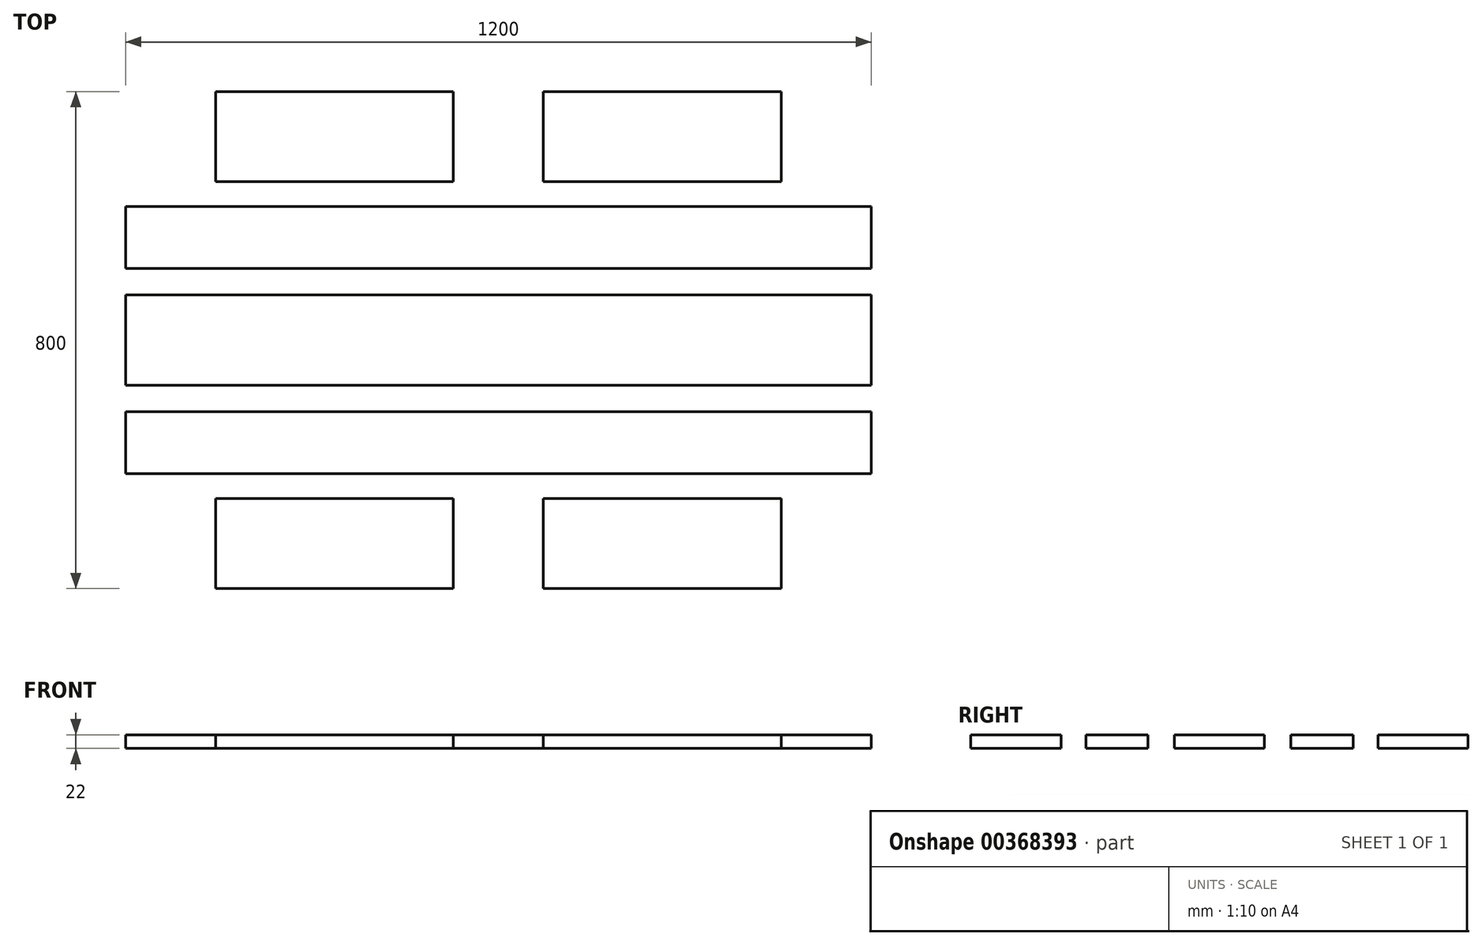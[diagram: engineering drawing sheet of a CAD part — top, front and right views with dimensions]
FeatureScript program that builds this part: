
annotation { "Feature Type Name" : "Feature", "Feature Type Description" : "" }
export const myFeature = defineFeature(function(context is Context, id is Id, definition is map)
    precondition{}
    {
        {
            var Q0;
            Q0=qCreatedBy(makeId("Top.planeOp"),FACE);
            var sketch = newSketch(context, id + "F0", { "sketchPlane" : qUnion([Q0])});
            skLineSegment(sketch, "E0.bottom", {"start": v(600, 400) * mm, "end": v(-600, 400) * mm, "construction": true});
            skLineSegment(sketch, "E0.top", {"start": v(600, -400) * mm, "end": v(-600, -400) * mm, "construction": true});
            skLineSegment(sketch, "E0.left", {"start": v(600, 400) * mm, "end": v(600, -400) * mm, "construction": true});
            skLineSegment(sketch, "E0.right", {"start": v(-600, 400) * mm, "end": v(-600, -400) * mm, "construction": true});
            skPoint(sketch, "E0.middle", {"position": v(0, 0) * mm});
            skLineSegment(sketch, "E1.left", {"start": v(-600, -400) * mm, "end": v(-600, -400) * mm});
            skLineSegment(sketch, "E1.right", {"start": v(600, -400) * mm, "end": v(600, -400) * mm});
            skLineSegment(sketch, "E2.bottom", {"start": v(-600, -400) * mm, "end": v(600, -400) * mm});
            skLineSegment(sketch, "E2.top", {"start": v(-600, -255) * mm, "end": v(600, -255) * mm});
            skLineSegment(sketch, "E2.left", {"start": v(-600, -400) * mm, "end": v(-600, -255) * mm});
            skLineSegment(sketch, "E2.right", {"start": v(600, -400) * mm, "end": v(600, -255) * mm});
            skLineSegment(sketch, "E3.bottom", {"start": v(-600, 400) * mm, "end": v(600, 400) * mm});
            skLineSegment(sketch, "E3.top", {"start": v(-600, 255) * mm, "end": v(600, 255) * mm});
            skLineSegment(sketch, "E3.left", {"start": v(-600, 400) * mm, "end": v(-600, 255) * mm});
            skLineSegment(sketch, "E3.right", {"start": v(600, 400) * mm, "end": v(600, 255) * mm});
            skLineSegment(sketch, "E4.bottom", {"start": v(-600, 72.5) * mm, "end": v(600, 72.5) * mm});
            skLineSegment(sketch, "E4.top", {"start": v(-600, -72.5) * mm, "end": v(600, -72.5) * mm});
            skLineSegment(sketch, "E4.left", {"start": v(-600, 72.5) * mm, "end": v(-600, -72.5) * mm});
            skLineSegment(sketch, "E4.right", {"start": v(600, 72.5) * mm, "end": v(600, -72.5) * mm});
            skLineSegment(sketch, "E5.bottom", {"start": v(-600, 215) * mm, "end": v(600, 215) * mm});
            skLineSegment(sketch, "E5.top", {"start": v(-600, 115) * mm, "end": v(600, 115) * mm});
            skLineSegment(sketch, "E5.left", {"start": v(-600, 215) * mm, "end": v(-600, 115) * mm});
            skLineSegment(sketch, "E5.right", {"start": v(600, 215) * mm, "end": v(600, 115) * mm});
            skLineSegment(sketch, "E6.bottom", {"start": v(-600, -115) * mm, "end": v(600, -115) * mm});
            skLineSegment(sketch, "E6.top", {"start": v(-600, -215) * mm, "end": v(600, -215) * mm});
            skLineSegment(sketch, "E6.left", {"start": v(-600, -115) * mm, "end": v(-600, -215) * mm});
            skLineSegment(sketch, "E6.right", {"start": v(600, -115) * mm, "end": v(600, -215) * mm});
            skLineSegment(sketch, "E7.bottom", {"start": v(-600, 400) * mm, "end": v(-455, 400) * mm});
            skLineSegment(sketch, "E7.top", {"start": v(-600, -400) * mm, "end": v(-455, -400) * mm});
            skLineSegment(sketch, "E7.left", {"start": v(-600, 400) * mm, "end": v(-600, -400) * mm});
            skLineSegment(sketch, "E7.right", {"start": v(-455, 400) * mm, "end": v(-455, -400) * mm});
            skLineSegment(sketch, "E8.bottom", {"start": v(600, 400) * mm, "end": v(455, 400) * mm});
            skLineSegment(sketch, "E8.top", {"start": v(600, -400) * mm, "end": v(455, -400) * mm});
            skLineSegment(sketch, "E8.left", {"start": v(600, 400) * mm, "end": v(600, -400) * mm});
            skLineSegment(sketch, "E8.right", {"start": v(455, 400) * mm, "end": v(455, -400) * mm});
            skLineSegment(sketch, "E9.bottom", {"start": v(72, -400) * mm, "end": v(-73, -400) * mm});
            skLineSegment(sketch, "E9.top", {"start": v(72, 400) * mm, "end": v(-73, 400) * mm});
            skLineSegment(sketch, "E9.left", {"start": v(72, -400) * mm, "end": v(72, 400) * mm});
            skLineSegment(sketch, "E9.right", {"start": v(-73, -400) * mm, "end": v(-73, 400) * mm});
            skPoint(sketch, "E9.middle", {"position": v(-0.5, 0) * mm});
            skSolve(sketch);
        }
        {
            var Q0;
            {var subQ5=sQuery(id+"F0.wireOp",EDGE,"E8.bottom");Q0=makeQuery(id+"F0.imprint","IMPRINT",FACE,{"disambiguationData":[TD([[makeQuery(id+"F0.imprint","IMPRINT",EDGE,{"derivedFrom":subQ5}),1.0]])]});}
            var Q1;
            {var subQ3=sQuery(id+"F0.wireOp",EDGE,"E9.left");var subQ5=sQuery(id+"F0.wireOp",EDGE,"E3.top");var subQ6=makeQuery(id+"F0.imprint","INTERSECT",VERTEX,{"derivedFrom":[subQ5,subQ3]});Q1=makeQuery(id+"F0.imprint","IMPRINT",FACE,{"disambiguationData":[TD([[makeQuery(id+"F0.imprint","IMPRINT",EDGE,{"disambiguationData":[TD([[subQ6,-1.0]])],"derivedFrom":subQ5}),1.0]])]});}
            var Q2;
            {var subQ5=sQuery(id+"F0.wireOp",EDGE,"E9.top");Q2=makeQuery(id+"F0.imprint","IMPRINT",FACE,{"disambiguationData":[TD([[makeQuery(id+"F0.imprint","IMPRINT",EDGE,{"derivedFrom":subQ5}),1.0]])]});}
            var Q3;
            {var subQ0=sQuery(id+"F0.wireOp",EDGE,"E7.right");var subQ5=sQuery(id+"F0.wireOp",EDGE,"E3.top");var subQ6=makeQuery(id+"F0.imprint","INTERSECT",VERTEX,{"derivedFrom":[subQ5,subQ0]});Q3=makeQuery(id+"F0.imprint","IMPRINT",FACE,{"disambiguationData":[TD([[makeQuery(id+"F0.imprint","IMPRINT",EDGE,{"disambiguationData":[TD([[subQ6,-1.0]])],"derivedFrom":subQ5}),1.0]])]});}
            var Q4;
            {var subQ5=sQuery(id+"F0.wireOp",EDGE,"E7.bottom");Q4=makeQuery(id+"F0.imprint","IMPRINT",FACE,{"disambiguationData":[TD([[makeQuery(id+"F0.imprint","IMPRINT",EDGE,{"derivedFrom":subQ5}),-1.0]])]});}
            var Q5;
            {var subQ0=sQuery(id+"F0.wireOp",EDGE,"E7.left");var subQ1=sQuery(id+"F0.wireOp",EDGE,"E5.bottom");var subQ2=makeQuery(id+"F0.imprint","INTERSECT",VERTEX,{"derivedFrom":[subQ1,subQ0]});Q5=makeQuery(id+"F0.imprint","IMPRINT",FACE,{"disambiguationData":[TD([[makeQuery(id+"F0.imprint","IMPRINT",EDGE,{"disambiguationData":[TD([[subQ2,-1.0]])],"derivedFrom":subQ1}),-1.0]])]});}
            var Q6;
            {var subQ0=sQuery(id+"F0.wireOp",EDGE,"E7.right");var subQ1=sQuery(id+"F0.wireOp",EDGE,"E5.bottom");var subQ2=makeQuery(id+"F0.imprint","INTERSECT",VERTEX,{"derivedFrom":[subQ1,subQ0]});Q6=makeQuery(id+"F0.imprint","IMPRINT",FACE,{"disambiguationData":[TD([[makeQuery(id+"F0.imprint","IMPRINT",EDGE,{"disambiguationData":[TD([[subQ2,-1.0]])],"derivedFrom":subQ1}),-1.0]])]});}
            var Q7;
            {var subQ0=sQuery(id+"F0.wireOp",EDGE,"E9.right");var subQ1=sQuery(id+"F0.wireOp",EDGE,"E5.bottom");var subQ2=makeQuery(id+"F0.imprint","INTERSECT",VERTEX,{"derivedFrom":[subQ1,subQ0]});Q7=makeQuery(id+"F0.imprint","IMPRINT",FACE,{"disambiguationData":[TD([[makeQuery(id+"F0.imprint","IMPRINT",EDGE,{"disambiguationData":[TD([[subQ2,-1.0]])],"derivedFrom":subQ1}),-1.0]])]});}
            var Q8;
            {var subQ0=sQuery(id+"F0.wireOp",EDGE,"E9.left");var subQ1=sQuery(id+"F0.wireOp",EDGE,"E5.bottom");var subQ2=makeQuery(id+"F0.imprint","INTERSECT",VERTEX,{"derivedFrom":[subQ1,subQ0]});Q8=makeQuery(id+"F0.imprint","IMPRINT",FACE,{"disambiguationData":[TD([[makeQuery(id+"F0.imprint","IMPRINT",EDGE,{"disambiguationData":[TD([[subQ2,-1.0]])],"derivedFrom":subQ1}),-1.0]])]});}
            var Q9;
            {var subQ0=sQuery(id+"F0.wireOp",EDGE,"E8.left");var subQ1=sQuery(id+"F0.wireOp",EDGE,"E5.bottom");var subQ2=makeQuery(id+"F0.imprint","INTERSECT",VERTEX,{"derivedFrom":[subQ1,subQ0]});Q9=makeQuery(id+"F0.imprint","IMPRINT",FACE,{"disambiguationData":[TD([[makeQuery(id+"F0.imprint","IMPRINT",EDGE,{"disambiguationData":[TD([[subQ2,1.0]])],"derivedFrom":subQ1}),-1.0]])]});}
            var Q10;
            {var subQ0=sQuery(id+"F0.wireOp",EDGE,"E8.left");var subQ1=sQuery(id+"F0.wireOp",EDGE,"E4.bottom");var subQ2=makeQuery(id+"F0.imprint","INTERSECT",VERTEX,{"derivedFrom":[subQ1,subQ0]});Q10=makeQuery(id+"F0.imprint","IMPRINT",FACE,{"disambiguationData":[TD([[makeQuery(id+"F0.imprint","IMPRINT",EDGE,{"disambiguationData":[TD([[subQ2,1.0]])],"derivedFrom":subQ1}),-1.0]])]});}
            var Q11;
            {var subQ0=sQuery(id+"F0.wireOp",EDGE,"E9.left");var subQ1=sQuery(id+"F0.wireOp",EDGE,"E4.bottom");var subQ2=makeQuery(id+"F0.imprint","INTERSECT",VERTEX,{"derivedFrom":[subQ1,subQ0]});Q11=makeQuery(id+"F0.imprint","IMPRINT",FACE,{"disambiguationData":[TD([[makeQuery(id+"F0.imprint","IMPRINT",EDGE,{"disambiguationData":[TD([[subQ2,-1.0]])],"derivedFrom":subQ1}),-1.0]])]});}
            var Q12;
            {var subQ0=sQuery(id+"F0.wireOp",EDGE,"E9.right");var subQ1=sQuery(id+"F0.wireOp",EDGE,"E4.bottom");var subQ2=makeQuery(id+"F0.imprint","INTERSECT",VERTEX,{"derivedFrom":[subQ1,subQ0]});Q12=makeQuery(id+"F0.imprint","IMPRINT",FACE,{"disambiguationData":[TD([[makeQuery(id+"F0.imprint","IMPRINT",EDGE,{"disambiguationData":[TD([[subQ2,-1.0]])],"derivedFrom":subQ1}),-1.0]])]});}
            var Q13;
            {var subQ0=sQuery(id+"F0.wireOp",EDGE,"E7.right");var subQ1=sQuery(id+"F0.wireOp",EDGE,"E4.bottom");var subQ2=makeQuery(id+"F0.imprint","INTERSECT",VERTEX,{"derivedFrom":[subQ1,subQ0]});Q13=makeQuery(id+"F0.imprint","IMPRINT",FACE,{"disambiguationData":[TD([[makeQuery(id+"F0.imprint","IMPRINT",EDGE,{"disambiguationData":[TD([[subQ2,-1.0]])],"derivedFrom":subQ1}),-1.0]])]});}
            var Q14;
            {var subQ0=sQuery(id+"F0.wireOp",EDGE,"E7.left");var subQ1=sQuery(id+"F0.wireOp",EDGE,"E4.bottom");var subQ2=makeQuery(id+"F0.imprint","INTERSECT",VERTEX,{"derivedFrom":[subQ1,subQ0]});Q14=makeQuery(id+"F0.imprint","IMPRINT",FACE,{"disambiguationData":[TD([[makeQuery(id+"F0.imprint","IMPRINT",EDGE,{"disambiguationData":[TD([[subQ2,-1.0]])],"derivedFrom":subQ1}),-1.0]])]});}
            var Q15;
            {var subQ0=sQuery(id+"F0.wireOp",EDGE,"E7.left");var subQ1=sQuery(id+"F0.wireOp",EDGE,"E6.bottom");var subQ2=makeQuery(id+"F0.imprint","INTERSECT",VERTEX,{"derivedFrom":[subQ1,subQ0]});Q15=makeQuery(id+"F0.imprint","IMPRINT",FACE,{"disambiguationData":[TD([[makeQuery(id+"F0.imprint","IMPRINT",EDGE,{"disambiguationData":[TD([[subQ2,-1.0]])],"derivedFrom":subQ1}),-1.0]])]});}
            var Q16;
            {var subQ0=sQuery(id+"F0.wireOp",EDGE,"E7.right");var subQ1=sQuery(id+"F0.wireOp",EDGE,"E6.bottom");var subQ2=makeQuery(id+"F0.imprint","INTERSECT",VERTEX,{"derivedFrom":[subQ1,subQ0]});Q16=makeQuery(id+"F0.imprint","IMPRINT",FACE,{"disambiguationData":[TD([[makeQuery(id+"F0.imprint","IMPRINT",EDGE,{"disambiguationData":[TD([[subQ2,-1.0]])],"derivedFrom":subQ1}),-1.0]])]});}
            var Q17;
            {var subQ0=sQuery(id+"F0.wireOp",EDGE,"E9.right");var subQ1=sQuery(id+"F0.wireOp",EDGE,"E6.bottom");var subQ2=makeQuery(id+"F0.imprint","INTERSECT",VERTEX,{"derivedFrom":[subQ1,subQ0]});Q17=makeQuery(id+"F0.imprint","IMPRINT",FACE,{"disambiguationData":[TD([[makeQuery(id+"F0.imprint","IMPRINT",EDGE,{"disambiguationData":[TD([[subQ2,-1.0]])],"derivedFrom":subQ1}),-1.0]])]});}
            var Q18;
            {var subQ0=sQuery(id+"F0.wireOp",EDGE,"E9.left");var subQ1=sQuery(id+"F0.wireOp",EDGE,"E6.bottom");var subQ2=makeQuery(id+"F0.imprint","INTERSECT",VERTEX,{"derivedFrom":[subQ1,subQ0]});Q18=makeQuery(id+"F0.imprint","IMPRINT",FACE,{"disambiguationData":[TD([[makeQuery(id+"F0.imprint","IMPRINT",EDGE,{"disambiguationData":[TD([[subQ2,-1.0]])],"derivedFrom":subQ1}),-1.0]])]});}
            var Q19;
            {var subQ0=sQuery(id+"F0.wireOp",EDGE,"E8.left");var subQ1=sQuery(id+"F0.wireOp",EDGE,"E6.bottom");var subQ2=makeQuery(id+"F0.imprint","INTERSECT",VERTEX,{"derivedFrom":[subQ1,subQ0]});Q19=makeQuery(id+"F0.imprint","IMPRINT",FACE,{"disambiguationData":[TD([[makeQuery(id+"F0.imprint","IMPRINT",EDGE,{"disambiguationData":[TD([[subQ2,1.0]])],"derivedFrom":subQ1}),-1.0]])]});}
            var Q20;
            {var subQ5=sQuery(id+"F0.wireOp",EDGE,"E8.top");Q20=makeQuery(id+"F0.imprint","IMPRINT",FACE,{"disambiguationData":[TD([[makeQuery(id+"F0.imprint","IMPRINT",EDGE,{"derivedFrom":subQ5}),-1.0]])]});}
            var Q21;
            {var subQ3=sQuery(id+"F0.wireOp",EDGE,"E9.left");var subQ5=sQuery(id+"F0.wireOp",EDGE,"E2.top");var subQ6=makeQuery(id+"F0.imprint","INTERSECT",VERTEX,{"derivedFrom":[subQ5,subQ3]});Q21=makeQuery(id+"F0.imprint","IMPRINT",FACE,{"disambiguationData":[TD([[makeQuery(id+"F0.imprint","IMPRINT",EDGE,{"disambiguationData":[TD([[subQ6,-1.0]])],"derivedFrom":subQ5}),-1.0]])]});}
            var Q22;
            {var subQ5=sQuery(id+"F0.wireOp",EDGE,"E9.bottom");Q22=makeQuery(id+"F0.imprint","IMPRINT",FACE,{"disambiguationData":[TD([[makeQuery(id+"F0.imprint","IMPRINT",EDGE,{"derivedFrom":subQ5}),-1.0]])]});}
            var Q23;
            {var subQ0=sQuery(id+"F0.wireOp",EDGE,"E7.right");var subQ5=sQuery(id+"F0.wireOp",EDGE,"E2.top");var subQ7=makeQuery(id+"F0.imprint","INTERSECT",VERTEX,{"derivedFrom":[subQ5,subQ0]});Q23=makeQuery(id+"F0.imprint","IMPRINT",FACE,{"disambiguationData":[TD([[makeQuery(id+"F0.imprint","IMPRINT",EDGE,{"disambiguationData":[TD([[subQ7,-1.0]])],"derivedFrom":subQ5}),-1.0]])]});}
            var Q24;
            {var subQ5=sQuery(id+"F0.wireOp",EDGE,"E7.top");Q24=makeQuery(id+"F0.imprint","IMPRINT",FACE,{"disambiguationData":[TD([[makeQuery(id+"F0.imprint","IMPRINT",EDGE,{"derivedFrom":subQ5}),1.0]])]});}
            extrude(context, id + "F1", {"entities" : qUnion([Q0, Q1, Q2, Q3, Q4, Q5, Q6, Q7, Q8, Q9, Q10, Q11, Q12, Q13, Q14, Q15, Q16, Q17, Q18, Q19, Q20, Q21, Q22, Q23, Q24]), "depth" : 22 * mm});
        }
    });
